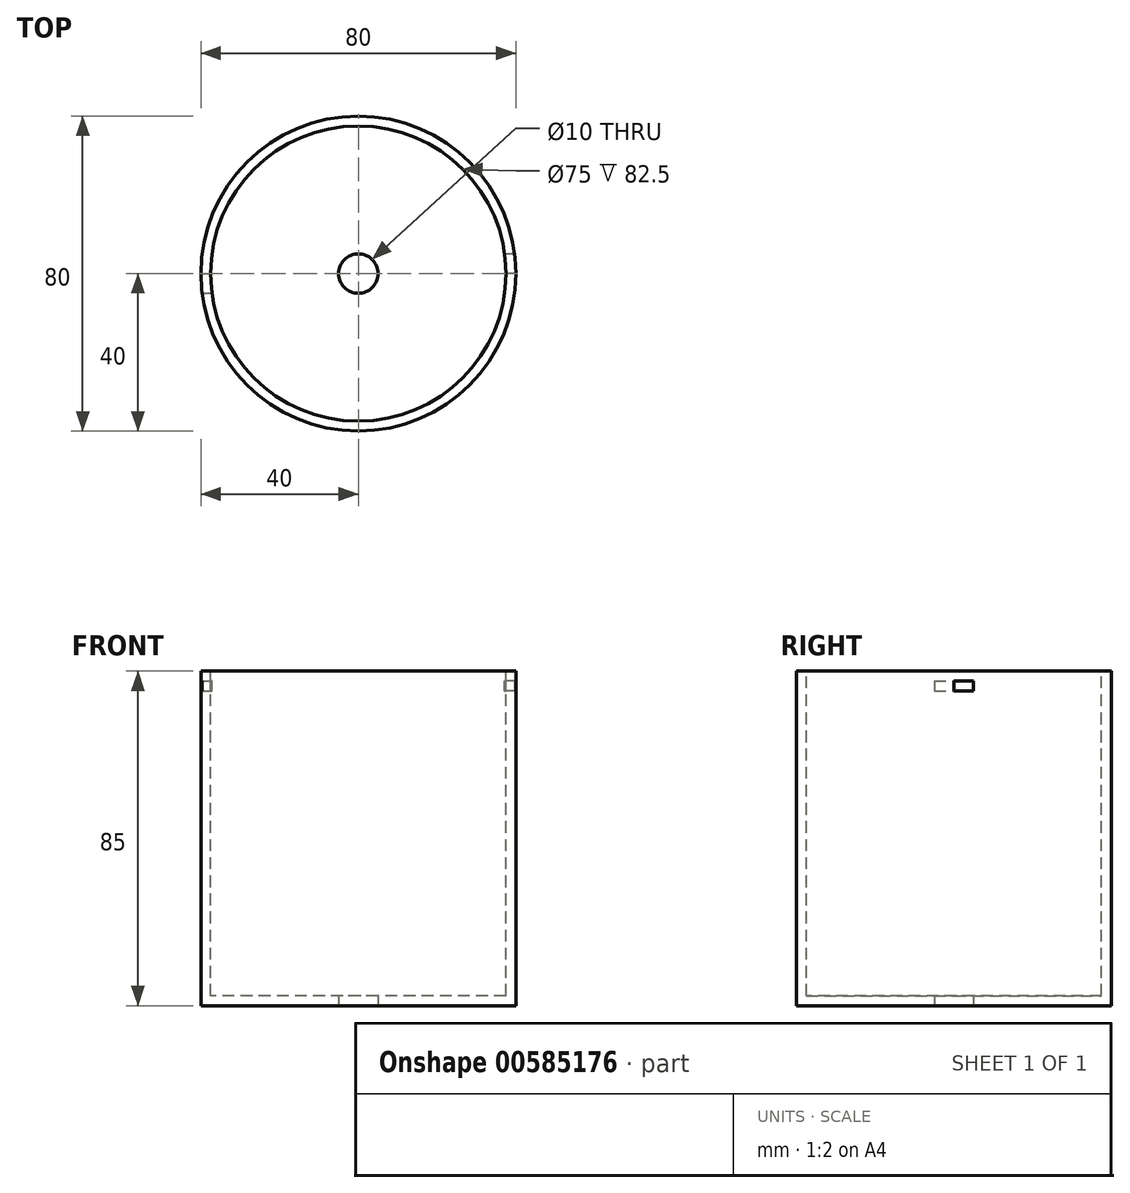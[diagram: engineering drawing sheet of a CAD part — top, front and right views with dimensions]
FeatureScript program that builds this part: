
annotation { "Feature Type Name" : "Feature", "Feature Type Description" : "" }
export const myFeature = defineFeature(function(context is Context, id is Id, definition is map)
    precondition{}
    {
        {
            var Q0;
            Q0=qCreatedBy(makeId("Top.planeOp"),FACE);
            var sketch = newSketch(context, id + "F0", { "sketchPlane" : qUnion([Q0])});
            skCircle(sketch, "E0", {"center": v(0, 0) * mm, "radius": 40 * mm});
            skCircle(sketch, "E1", {"center": v(0, 0) * mm, "radius": 5 * mm});
            skSolve(sketch);
        }
        {
            var Q0;
            Q0=makeQuery(id+"F0.imprint","IMPRINT",FACE,{"disambiguationData":[TD([[makeQuery(id+"F0.imprint","IMPRINT",EDGE,{"derivedFrom":sQuery(id+"F0.wireOp",EDGE,"E0")}),1.0]])]});
            extrude(context, id + "F1", {"entities" : qUnion([Q0]), "depth" : 85 * mm, "offsetDistance" : 25.4 * mm});
        }
        {
            var Q0;
            Q0=makeQuery(id+"F1.opExtrude","CAP_FACE",FACE,{"disambiguationData":[OSD([sQuery(id+"F0.wireOp",EDGE,"E0")])],"isStart":false});
            var sketch = newSketch(context, id + "F2", { "sketchPlane" : qUnion([Q0])});
            skSolve(sketch);
        }
        {
            var Q0;
            Q0=makeQuery(id+"F2.imprint","IMPRINT",FACE,{"disambiguationData":[TD([[makeQuery(id+"F2.imprint","IMPRINT",EDGE,{"derivedFrom":makeQuery(id+"F1.opExtrude","CAP_EDGE",EDGE,{"disambiguationData":[OSD([sQuery(id+"F0.wireOp",EDGE,"E0")])],"isStart":false})}),1.0]])]});
            var sketch = newSketch(context, id + "F3", { "sketchPlane" : qUnion([Q0])});
            skCircle(sketch, "E2", {"center": v(0, 0) * mm, "radius": 37.5 * mm});
            skSolve(sketch);
        }
        {
            var Q0;
            Q0=makeQuery(id+"F3.imprint","IMPRINT",FACE,{"disambiguationData":[TD([[makeQuery(id+"F3.imprint","IMPRINT",EDGE,{"derivedFrom":sQuery(id+"F3.wireOp",EDGE,"E2")}),1.0]])]});
            extrude(context, id + "F4", {"entities" : qUnion([Q0]), "operationType" : NewBodyOperationType.REMOVE, "oppositeDirection" : true, "depth" : 82.5 * mm, "offsetDistance" : 25.4 * mm});
        }
        {
            var Q0;
            Q0=qCreatedBy(makeId("Right.planeOp"),FACE);
            var sketch = newSketch(context, id + "F5", { "sketchPlane" : qUnion([Q0])});
            skLineSegment(sketch, "E3", {"start": v(0, 0) * mm, "end": v(0, 85) * mm});
            skLineSegment(sketch, "E4", {"start": v(0, 85) * mm, "end": v(-40, 85) * mm});
            skLineSegment(sketch, "E5.bottom", {"start": v(-40, 85) * mm, "end": v(-5, 85) * mm});
            skLineSegment(sketch, "E5.top", {"start": v(-40, 80) * mm, "end": v(-5, 80) * mm});
            skLineSegment(sketch, "E5.left", {"start": v(-40, 85) * mm, "end": v(-40, 80) * mm});
            skLineSegment(sketch, "E5.right", {"start": v(-5, 85) * mm, "end": v(-5, 80) * mm});
            skLineSegment(sketch, "E6", {"start": v(0, 85) * mm, "end": v(40, 85) * mm});
            skLineSegment(sketch, "E7.bottom", {"start": v(40, 85) * mm, "end": v(5, 85) * mm});
            skLineSegment(sketch, "E7.top", {"start": v(40, 80) * mm, "end": v(5, 80) * mm});
            skLineSegment(sketch, "E7.left", {"start": v(40, 85) * mm, "end": v(40, 80) * mm});
            skLineSegment(sketch, "E7.right", {"start": v(5, 85) * mm, "end": v(5, 80) * mm});
            skLineSegment(sketch, "E8.bottom", {"start": v(5, 80) * mm, "end": v(0, 80) * mm});
            skLineSegment(sketch, "E8.top", {"start": v(5, 82.5) * mm, "end": v(0, 82.5) * mm});
            skLineSegment(sketch, "E8.left", {"start": v(5, 80) * mm, "end": v(5, 82.5) * mm});
            skLineSegment(sketch, "E8.right", {"start": v(0, 80) * mm, "end": v(0, 82.5) * mm});
            skSolve(sketch);
        }
        {
            var Q0;
            Q0=makeQuery(id+"F5.imprint","IMPRINT",FACE,{"disambiguationData":[TD([[makeQuery(id+"F5.imprint","IMPRINT",EDGE,{"derivedFrom":sQuery(id+"F5.wireOp",EDGE,"E7.bottom")}),1.0]])]});
            var Q1;
            Q1=makeQuery(id+"F5.imprint","IMPRINT",FACE,{"disambiguationData":[TD([[makeQuery(id+"F5.imprint","IMPRINT",EDGE,{"derivedFrom":sQuery(id+"F5.wireOp",EDGE,"E8.bottom")}),-1.0]])]});
            var Q2;
            Q2=makeQuery(id+"F5.imprint","IMPRINT",FACE,{"disambiguationData":[TD([[makeQuery(id+"F5.imprint","IMPRINT",EDGE,{"derivedFrom":sQuery(id+"F5.wireOp",EDGE,"E5.bottom")}),-1.0]])]});
            extrude(context, id + "F6", {"entities" : qUnion([Q0, Q1, Q2]), "depth" : 50 * mm, "offsetDistance" : 25 * mm});
        }
        {
            var Q0;
            Q0=qCreatedBy(makeId("Right.planeOp"),FACE);
            var sketch = newSketch(context, id + "F7", { "sketchPlane" : qUnion([Q0])});
            skLineSegment(sketch, "E9", {"start": v(0, 0) * mm, "end": v(0, 85.17) * mm});
            skSolve(sketch);
        }
        {
            var Q0;
            Q0=makeQuery(id+"F6.opExtrude","SWEPT_BODY",BODY,{"disambiguationData":[OSD([sQuery(id+"F5.wireOp",EDGE,"E5.bottom"),sQuery(id+"F5.wireOp",EDGE,"E5.top"),sQuery(id+"F5.wireOp",EDGE,"E5.left"),sQuery(id+"F5.wireOp",EDGE,"E5.right")])]});
            var Q1;
            Q1=makeQuery(id+"F6.opExtrude","SWEPT_BODY",BODY,{"disambiguationData":[OSD([sQuery(id+"F5.wireOp",EDGE,"E7.bottom"),sQuery(id+"F5.wireOp",EDGE,"E7.top"),sQuery(id+"F5.wireOp",EDGE,"E7.left"),sQuery(id+"F5.wireOp",EDGE,"E7.right"),sQuery(id+"F5.wireOp",EDGE,"E8.bottom"),sQuery(id+"F5.wireOp",EDGE,"E8.top"),sQuery(id+"F5.wireOp",EDGE,"E8.right")])]});
            var Q2;
            Q2=sQuery(id+"F7.wireOp",EDGE,"E9");
            circularPattern(context, id + "F8", {"entities" : qUnion([Q0, Q1]), "axis" : qUnion([Q2]), "angle" : 360 * degree, "instanceCount" : 2, "equalSpace" : true});
        }
        {
            var Q0;
            Q0=makeQuery(id+"F6.opExtrude","SWEPT_BODY",BODY,{"disambiguationData":[OSD([sQuery(id+"F5.wireOp",EDGE,"E5.bottom"),sQuery(id+"F5.wireOp",EDGE,"E5.top"),sQuery(id+"F5.wireOp",EDGE,"E5.left"),sQuery(id+"F5.wireOp",EDGE,"E5.right")])]});
            var Q1;
            Q1=makeQuery(id+"F6.opExtrude","SWEPT_BODY",BODY,{"disambiguationData":[OSD([sQuery(id+"F5.wireOp",EDGE,"E7.bottom"),sQuery(id+"F5.wireOp",EDGE,"E7.top"),sQuery(id+"F5.wireOp",EDGE,"E7.left"),sQuery(id+"F5.wireOp",EDGE,"E7.right"),sQuery(id+"F5.wireOp",EDGE,"E8.bottom"),sQuery(id+"F5.wireOp",EDGE,"E8.top"),sQuery(id+"F5.wireOp",EDGE,"E8.right")])]});
            var Q2;
            Q2=makeQuery(id+"F8.opPattern","COPY",BODY,{"derivedFrom":makeQuery(id+"F6.opExtrude","SWEPT_BODY",BODY,{"disambiguationData":[OSD([sQuery(id+"F5.wireOp",EDGE,"E5.bottom"),sQuery(id+"F5.wireOp",EDGE,"E5.top"),sQuery(id+"F5.wireOp",EDGE,"E5.left"),sQuery(id+"F5.wireOp",EDGE,"E5.right")])]}),"instanceName":"1"});
            var Q3;
            Q3=makeQuery(id+"F8.opPattern","COPY",BODY,{"derivedFrom":makeQuery(id+"F6.opExtrude","SWEPT_BODY",BODY,{"disambiguationData":[OSD([sQuery(id+"F5.wireOp",EDGE,"E7.bottom"),sQuery(id+"F5.wireOp",EDGE,"E7.top"),sQuery(id+"F5.wireOp",EDGE,"E7.left"),sQuery(id+"F5.wireOp",EDGE,"E7.right"),sQuery(id+"F5.wireOp",EDGE,"E8.bottom"),sQuery(id+"F5.wireOp",EDGE,"E8.top"),sQuery(id+"F5.wireOp",EDGE,"E8.right")])]}),"instanceName":"1"});
            var Q4;
            Q4=makeQuery(id+"F1.opExtrude","SWEPT_BODY",BODY,{"disambiguationData":[OSD([sQuery(id+"F0.wireOp",EDGE,"E0"),sQuery(id+"F0.wireOp",EDGE,"E1")])]});
            booleanBodies(context, id + "F9", {"operationType" : BooleanOperationType.SUBTRACTION, "tools" : qUnion([Q0, Q1, Q2, Q3]), "targets" : qUnion([Q4])});
        }
    });
